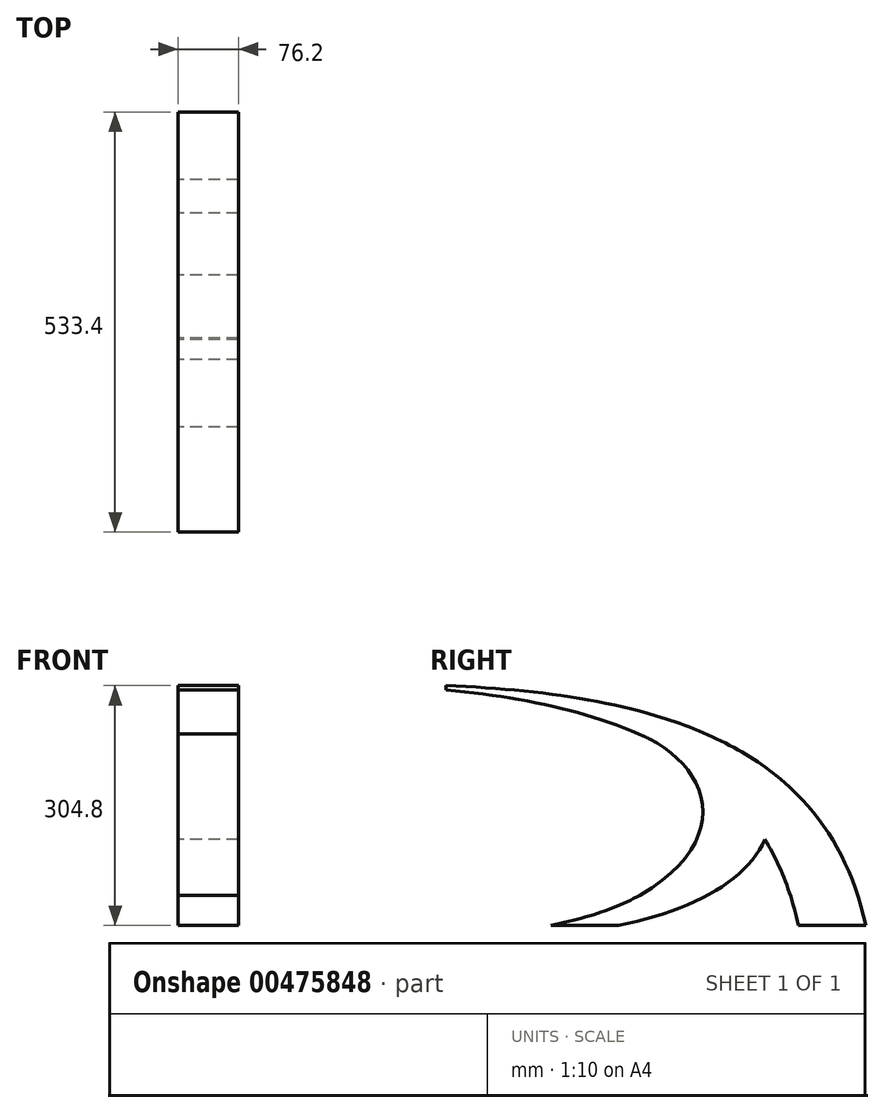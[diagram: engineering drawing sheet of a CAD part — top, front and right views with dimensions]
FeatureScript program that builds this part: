
annotation { "Feature Type Name" : "Feature", "Feature Type Description" : "" }
export const myFeature = defineFeature(function(context is Context, id is Id, definition is map)
    precondition{}
    {
        {
            var Q0;
            Q0=qCreatedBy(makeId("Right.planeOp"),FACE);
            var sketch = newSketch(context, id + "F0", { "sketchPlane" : qUnion([Q0])});
            skFitSpline(sketch, "E0", {"points": [v(226.4, -123.17) * mm, v(-307, 181.63) * mm], "startDerivative": vector(-152.15, 697.22) * mm, "endDerivative": vector(-800.1, 34.28) * mm});
            skFitSpline(sketch, "E1", {"points": [v(-40.3, 143.24) * mm, v(-173.65, -123.17) * mm], "startDerivative": vector(386.18, -408.72) * mm, "endDerivative": vector(-505.78, -101) * mm});
            skFitSpline(sketch, "E2", {"points": [v(45.43, 143.24) * mm, v(-87.92, -123.17) * mm], "startDerivative": vector(386.18, -408.72) * mm, "endDerivative": vector(-505.78, -101) * mm});
            skFitSpline(sketch, "E3", {"points": [v(140.68, -123.17) * mm, v(-392.72, 181.63) * mm], "startDerivative": vector(-152.15, 697.22) * mm, "endDerivative": vector(-800.1, 34.28) * mm});
            skFitSpline(sketch, "E4", {"points": [v(-62.31, 120.1) * mm, v(-60.29, -84.74) * mm], "startDerivative": vector(258.37, -104.87) * mm, "endDerivative": vector(-378.53, -222.19) * mm});
            skLineSegment(sketch, "E5", {"start": v(-307, 181.63) * mm, "end": v(-307, 175.93) * mm});
            skLineSegment(sketch, "E6", {"start": v(-173.65, -123.17) * mm, "end": v(-87.92, -123.17) * mm});
            skLineSegment(sketch, "E7", {"start": v(140.68, -123.17) * mm, "end": v(226.4, -123.17) * mm});
            skSolve(sketch);
        }
        {
            var Q0;
            {var subQ0=sQuery(id+"F0.wireOp",EDGE,"E1");var subQ1=sQuery(id+"F0.wireOp",EDGE,"E0");var subQ2=makeQuery(id+"F0.imprint","INTERSECT",VERTEX,{"derivedFrom":[subQ1,subQ0]});Q0=makeQuery(id+"F0.imprint","IMPRINT",FACE,{"disambiguationData":[TD([[makeQuery(id+"F0.imprint","IMPRINT",EDGE,{"disambiguationData":[TD([[subQ2,1.0]])],"derivedFrom":subQ1}),1.0]])]});}
            var Q1;
            {var subQ0=sQuery(id+"F0.wireOp",EDGE,"E7");Q1=makeQuery(id+"F0.imprint","IMPRINT",FACE,{"disambiguationData":[TD([[makeQuery(id+"F0.imprint","IMPRINT",EDGE,{"derivedFrom":subQ0}),1.0]])]});}
            var Q2;
            {var subQ8=sQuery(id+"F0.wireOp",EDGE,"E5");Q2=makeQuery(id+"F0.imprint","IMPRINT",FACE,{"disambiguationData":[TD([[makeQuery(id+"F0.imprint","IMPRINT",EDGE,{"derivedFrom":subQ8}),1.0]])]});}
            var Q3;
            {var subQ0=sQuery(id+"F0.wireOp",EDGE,"E4");var subQ1=sQuery(id+"F0.wireOp",EDGE,"E1");var subQ2=makeQuery(id+"F0.imprint","INTERSECT",VERTEX,{"derivedFrom":[subQ1,subQ0]});Q3=makeQuery(id+"F0.imprint","IMPRINT",FACE,{"disambiguationData":[TD([[makeQuery(id+"F0.imprint","IMPRINT",EDGE,{"disambiguationData":[TD([[subQ2,1.0]])],"derivedFrom":subQ1}),-1.0]])]});}
            var Q4;
            {var subQ0=sQuery(id+"F0.wireOp",EDGE,"E6");Q4=makeQuery(id+"F0.imprint","IMPRINT",FACE,{"disambiguationData":[TD([[makeQuery(id+"F0.imprint","IMPRINT",EDGE,{"derivedFrom":subQ0}),1.0]])]});}
            extrude(context, id + "F1", {"entities" : qUnion([Q0, Q1, Q2, Q3, Q4]), "depth" : 38.1 * mm, "hasSecondDirection" : true, "secondDirectionOppositeDirection" : true, "secondDirectionDepth" : 38.1 * mm});
        }
    });
